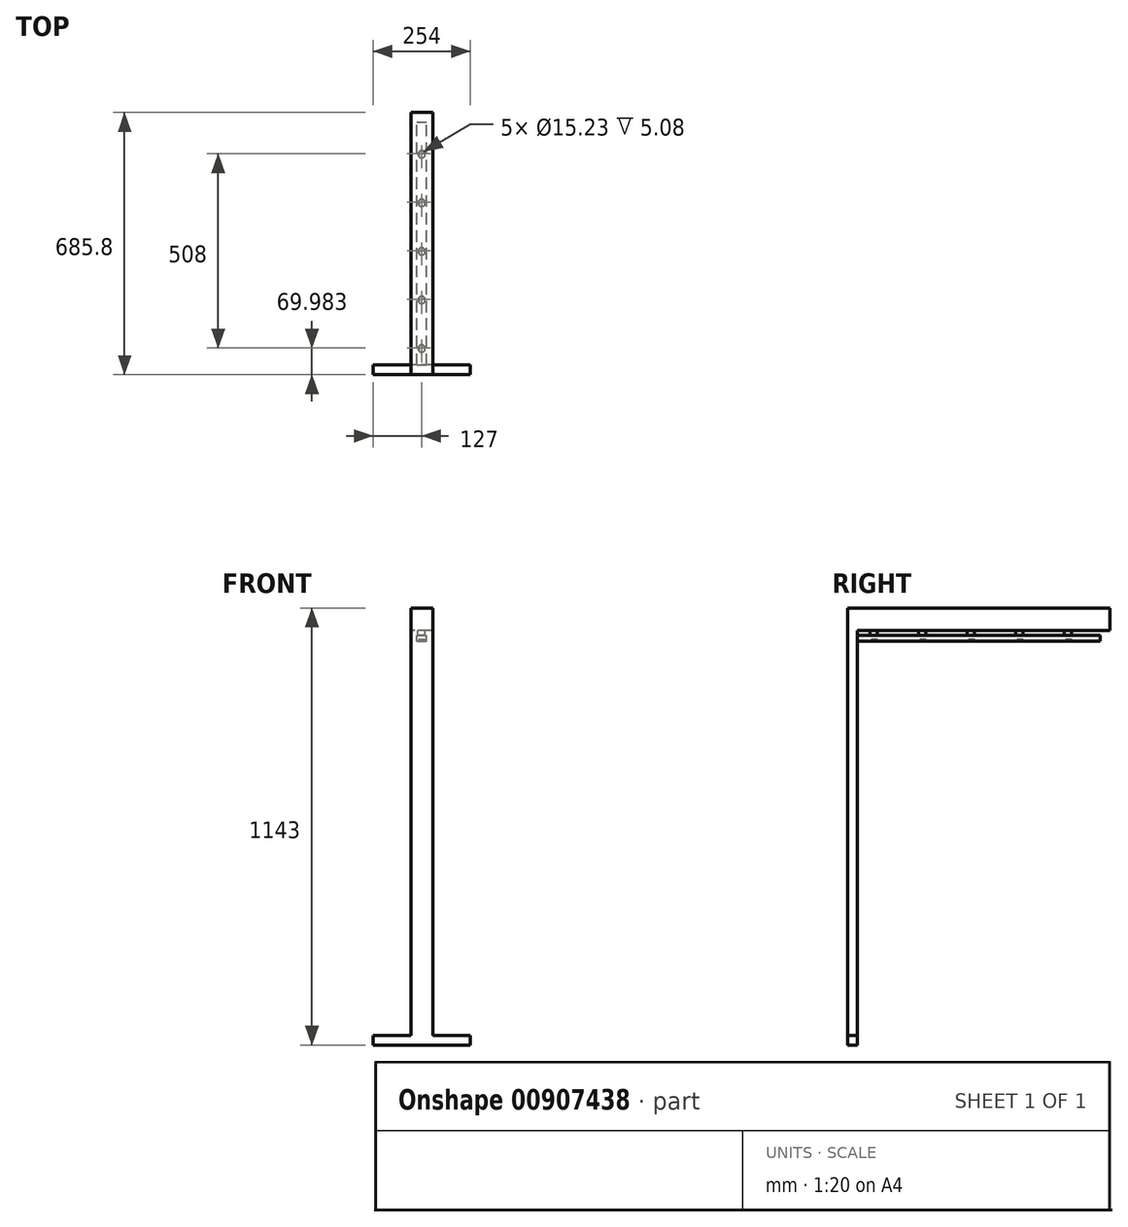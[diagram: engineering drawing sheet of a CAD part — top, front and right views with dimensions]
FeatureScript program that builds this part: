
annotation { "Feature Type Name" : "Feature", "Feature Type Description" : "" }
export const myFeature = defineFeature(function(context is Context, id is Id, definition is map)
    precondition{}
    {
        {
            var Q0;
            Q0=qCreatedBy(makeId("Front.planeOp"),FACE);
            var sketch = newSketch(context, id + "F0", { "sketchPlane" : qUnion([Q0])});
            skLineSegment(sketch, "E0.bottom", {"start": v(127, -12.7) * mm, "end": v(-127, -12.7) * mm});
            skLineSegment(sketch, "E0.top", {"start": v(127, 12.7) * mm, "end": v(-127, 12.7) * mm});
            skLineSegment(sketch, "E0.left", {"start": v(127, -12.7) * mm, "end": v(127, 12.7) * mm});
            skLineSegment(sketch, "E0.right", {"start": v(-127, -12.7) * mm, "end": v(-127, 12.7) * mm});
            skPoint(sketch, "E0.middle", {"position": v(0, 0) * mm});
            skSolve(sketch);
        }
        {
            var Q0;
            Q0 = qSketchRegion(id + "F0", true);
            extrude(context, id + "F1", {"entities" : qUnion([Q0]), "depth" : 25.4 * mm, "offsetDistance" : 25.4 * mm});
        }
        {
            var Q0;
            Q0=makeQuery(id+"F1.opExtrude","SWEPT_FACE",FACE,{"disambiguationData":[OSD([sQuery(id+"F0.wireOp",EDGE,"E0.top")])]});
            var sketch = newSketch(context, id + "F2", { "sketchPlane" : qUnion([Q0])});
            skLineSegment(sketch, "E1.bottom", {"start": v(-28.4, 0) * mm, "end": v(28.8, 0) * mm});
            skLineSegment(sketch, "E1.top", {"start": v(-28.4, -25.4) * mm, "end": v(28.8, -25.4) * mm});
            skLineSegment(sketch, "E1.left", {"start": v(-28.4, 0) * mm, "end": v(-28.4, -25.4) * mm});
            skLineSegment(sketch, "E1.right", {"start": v(28.8, 0) * mm, "end": v(28.8, -25.4) * mm});
            skSolve(sketch);
        }
        {
            var Q0;
            Q0 = qSketchRegion(id + "F2", true);
            extrude(context, id + "F3", {"entities" : qUnion([Q0]), "operationType" : NewBodyOperationType.ADD, "depth" : 1117.6 * mm, "offsetDistance" : 25.4 * mm});
        }
        {
            var Q0;
            Q0=makeQuery(id+"F3.boolean.opBoolean","MERGE",FACE,{"derivedFrom":[makeQuery(id+"F1.opExtrude","CAP_FACE",FACE,{"disambiguationData":[OSD([sQuery(id+"F0.wireOp",EDGE,"E0.bottom"),sQuery(id+"F0.wireOp",EDGE,"E0.top"),sQuery(id+"F0.wireOp",EDGE,"E0.left"),sQuery(id+"F0.wireOp",EDGE,"E0.right")])],"isStart":true}),makeQuery(id+"F3.opExtrude","SWEPT_FACE",FACE,{"disambiguationData":[OSD([sQuery(id+"F2.wireOp",EDGE,"E1.bottom")])]})]});
            var sketch = newSketch(context, id + "F4", { "sketchPlane" : qUnion([Q0])});
            skLineSegment(sketch, "E2.bottom", {"start": v(-28.8, 1130.3) * mm, "end": v(28.4, 1130.3) * mm});
            skLineSegment(sketch, "E2.top", {"start": v(-28.8, 1070.89) * mm, "end": v(28.4, 1070.89) * mm});
            skLineSegment(sketch, "E2.left", {"start": v(-28.8, 1130.3) * mm, "end": v(-28.8, 1070.89) * mm});
            skLineSegment(sketch, "E2.right", {"start": v(28.4, 1130.3) * mm, "end": v(28.4, 1070.89) * mm});
            skSolve(sketch);
        }
        {
            var Q0;
            Q0 = qSketchRegion(id + "F4", true);
            extrude(context, id + "F5", {"entities" : qUnion([Q0]), "operationType" : NewBodyOperationType.ADD, "depth" : 660.4 * mm, "offsetDistance" : 25.4 * mm});
        }
        {
            var Q0;
            Q0=makeQuery(id+"F5.opExtrude","SWEPT_FACE",FACE,{"disambiguationData":[OSD([sQuery(id+"F4.wireOp",EDGE,"E2.top")])]});
            var sketch = newSketch(context, id + "F6", { "sketchPlane" : qUnion([Q0])});
            skLineSegment(sketch, "E3", {"start": v(0, 0) * mm, "end": v(0, -660.4) * mm, "construction": true});
            skCircle(sketch, "E4", {"center": v(0, -43.15) * mm, "radius": 9.53 * mm});
            skCircle(sketch, "E5.0.1.0", {"center": v(0, -170.15) * mm, "radius": 9.53 * mm});
            skCircle(sketch, "E5.0.2.0", {"center": v(0, -297.15) * mm, "radius": 9.53 * mm});
            skCircle(sketch, "E5.0.3.0", {"center": v(0, -424.15) * mm, "radius": 9.53 * mm});
            skCircle(sketch, "E5.0.4.0", {"center": v(0, -551.15) * mm, "radius": 9.53 * mm});
            skLineSegment(sketch, "E5.direction1", {"start": v(0, -43.15) * mm, "end": v(25.4, -43.15) * mm, "construction": true});
            skLineSegment(sketch, "E5.direction2", {"start": v(0, -43.15) * mm, "end": v(0, -170.15) * mm, "construction": true});
            skSolve(sketch);
        }
        {
            var Q0;
            Q0 = qSketchRegion(id + "F6", true);
            extrude(context, id + "F7", {"entities" : qUnion([Q0]), "operationType" : NewBodyOperationType.ADD, "depth" : 12.7 * mm, "offsetDistance" : 25.4 * mm});
        }
        {
            var Q0;
            Q0=makeQuery(id+"F7.opExtrude","CAP_FACE",FACE,{"disambiguationData":[OSD([sQuery(id+"F6.wireOp",EDGE,"E4")])],"isStart":false});
            var sketch = newSketch(context, id + "F8", { "sketchPlane" : qUnion([Q0])});
            skLineSegment(sketch, "E6.bottom", {"start": v(-12.82, 0) * mm, "end": v(12.58, 0) * mm});
            skLineSegment(sketch, "E6.top", {"start": v(-12.82, -635) * mm, "end": v(12.58, -635) * mm});
            skLineSegment(sketch, "E6.left", {"start": v(-12.82, 0) * mm, "end": v(-12.82, -635) * mm});
            skLineSegment(sketch, "E6.right", {"start": v(12.58, 0) * mm, "end": v(12.58, -635) * mm});
            skSolve(sketch);
        }
        {
            var Q0;
            Q0 = qSketchRegion(id + "F8", true);
            extrude(context, id + "F9", {"entities" : qUnion([Q0]), "operationType" : NewBodyOperationType.ADD, "depth" : 15.24 * mm, "offsetDistance" : 25.4 * mm});
        }
        {
            var Q0;
            Q0=makeQuery(id+"F9.opExtrude","CAP_FACE",FACE,{"disambiguationData":[OSD([sQuery(id+"F8.wireOp",EDGE,"E6.bottom"),sQuery(id+"F8.wireOp",EDGE,"E6.top"),sQuery(id+"F8.wireOp",EDGE,"E6.left"),sQuery(id+"F8.wireOp",EDGE,"E6.right")])],"isStart":false});
            var sketch = newSketch(context, id + "F10", { "sketchPlane" : qUnion([Q0])});
            skCircle(sketch, "E7", {"center": v(0, -44.58) * mm, "radius": 7.62 * mm});
            skCircle(sketch, "E8.0.1.0", {"center": v(0, -171.58) * mm, "radius": 7.62 * mm});
            skCircle(sketch, "E8.0.2.0", {"center": v(0, -298.58) * mm, "radius": 7.62 * mm});
            skCircle(sketch, "E8.0.3.0", {"center": v(0, -425.58) * mm, "radius": 7.62 * mm});
            skCircle(sketch, "E8.0.4.0", {"center": v(0, -552.58) * mm, "radius": 7.62 * mm});
            skLineSegment(sketch, "E8.direction1", {"start": v(0, -44.58) * mm, "end": v(25.4, -44.58) * mm, "construction": true});
            skLineSegment(sketch, "E8.direction2", {"start": v(0, -44.58) * mm, "end": v(0, -171.58) * mm, "construction": true});
            skSolve(sketch);
        }
        {
            var Q0;
            Q0 = qSketchRegion(id + "F10", true);
            extrude(context, id + "F11", {"entities" : qUnion([Q0]), "operationType" : NewBodyOperationType.REMOVE, "oppositeDirection" : true, "depth" : 5.08 * mm, "offsetDistance" : 25.4 * mm});
        }
    });
